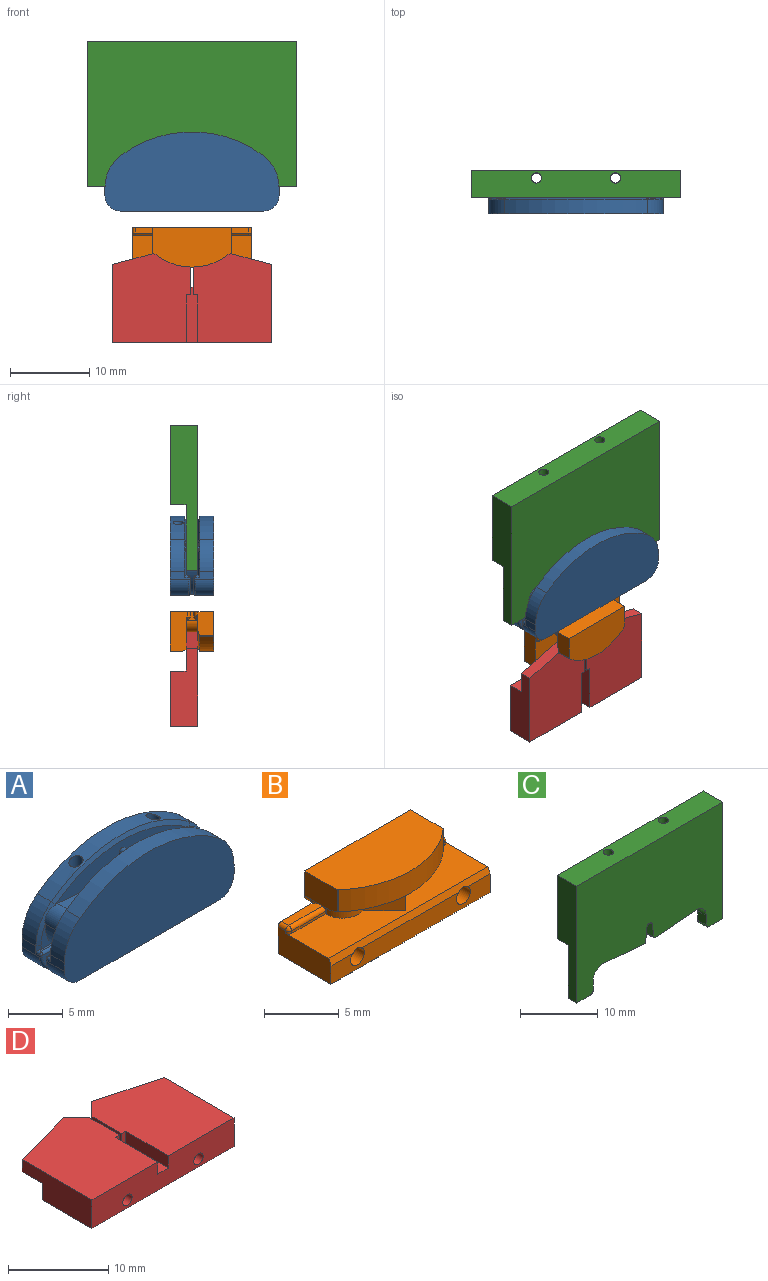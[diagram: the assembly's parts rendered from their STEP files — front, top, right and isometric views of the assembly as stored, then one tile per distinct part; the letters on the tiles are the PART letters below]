
ASSEMBLY  parts=4 mates=3
PART A: 86 faces, bbox 22.4x5.6x10.2 mm
  f0: plane 4.8x2mm, normal (0,1,0), area 5mm2, adj f8,f42,f82,f83,f84
  f1: plane 4.8x2mm, normal (0,-1,0), area 5mm2, adj f8,f46,f71,f72,f73
  f2: plane 2.56x1.23mm, normal (0,-1,0), area 1.6mm2, adj f8,f26,f56,f57
  f3: plane 2.56x1.23mm, normal (0,-1,0), area 1.6mm2, adj f9,f27,f53,f54
  f4: plane 2.56x1.23mm, normal (0,1,0), area 1.6mm2, adj f9,f38,f51,f52
  f5: plane 2.56x1.23mm, normal (0,1,0), area 1.6mm2, adj f8,f37,f48,f49
  f6: plane 17.45x3.56mm, normal (0,1,0), area 38.3mm2, adj f15,f16,f17,f18,f19,f20,f21,f22
  f7: plane 10x0.5mm, normal (0,0,-1), area 5mm2, adj f8,f9,f69,f80
  f8: cylinder r=5mm len=5mm, axis (0,1,0), area 6.7mm2, adj f0,f1,f2,f5,f7,f21,f26,f37
  f9: cylinder r=5mm len=5mm, axis (0,1,0), area 6.7mm2, adj f3,f4,f7,f22,f27,f28,f38,f39
  f10: plane 2.3x1mm, normal (-1,0,0), area 1.9mm2, adj f12,f34,f43,f48,f62,f84
  f11: plane 2.3x1mm, normal (1,0,0), area 1.9mm2, adj f12,f33,f40,f52,f63,f76
  f12: plane 22x10mm, normal (0,-1,0), area 184.3mm2, adj f10,f11,f30,f32,f33,f34,f62,f63
  f13: plane 17.45x3.56mm, normal (0,-1,0), area 38.3mm2, adj f15,f16,f17,f18,f19,f20,f21,f22
  f14: plane 22x10mm, normal (0,1,0), area 184.3mm2, adj f24,f25,f29,f31,f35,f36,f60,f61
  f15: cylinder r=0.5mm len=1.5mm, axis (0,1,0), area 1.2mm2, adj f6,f13,f16,f23
  f16: plane 1.94x1.5mm, normal (1,0,0.04), area 2.9mm2, adj f6,f13,f15,f17
  f17: cylinder r=0.35mm len=1.5mm, axis (0,1,0), area 1.6mm2, adj f6,f13,f16,f18
  f18: plane 1.94x1.5mm, normal (-1,0,0.04), area 2.9mm2, adj f6,f13,f17,f19
  f19: cylinder r=0.5mm len=1.5mm, axis (0,1,0), area 1.2mm2, adj f6,f13,f18,f20
  f20: plane 7.4x1.5mm, normal (0.09,0,1), area 11.1mm2, adj f6,f13,f19,f21
  f21: cylinder r=1.5mm len=1.63mm, axis (0,1,0), area 3.7mm2, adj f6,f8,f13,f20,f49,f56
  f22: cylinder r=1.5mm len=1.63mm, axis (0,1,0), area 3.7mm2, adj f6,f9,f13,f23,f51,f54
  f23: plane 7.4x1.5mm, normal (-0.09,0,1), area 11.1mm2, adj f6,f13,f15,f22
  f24: plane 2.3x1mm, normal (-1,0,0), area 1.9mm2, adj f14,f36,f47,f57,f61,f73
  f25: plane 2.3x1mm, normal (1,0,0), area 1.9mm2, adj f14,f35,f44,f53,f60,f65
  f26: plane 1.43x0.28mm, normal (0,0,1), area 0.3mm2, adj f2,f8,f46,f47,f57
  f27: plane 1.43x0.28mm, normal (0,0,1), area 0.3mm2, adj f3,f9,f44,f45,f53
  f28: plane 4.8x2mm, normal (0,-1,0), area 5mm2, adj f9,f45,f65,f66,f67
  f29: plane 18x2.33mm, normal (0,0,-1), area 39mm2, adj f14,f58,f59,f60,f61,f67,f68,f69
  f30: plane 18x2.33mm, normal (0,0,-1), area 41.7mm2, adj f12,f62,f63,f78,f79,f80,f81,f82
  f31: cylinder r=15mm len=18mm, axis (0,-1,0), area 31.9mm2, adj f14,f35,f36,f55,f58,f59
  f32: cylinder r=15mm len=18mm, axis (0,-1,0), area 34.7mm2, adj f12,f33,f34,f50
  f33: cylinder r=5mm len=4mm, axis (0,-1,0), area 8.3mm2, adj f11,f12,f32,f51
  f34: cylinder r=5mm len=4mm, axis (0,-1,0), area 8.3mm2, adj f10,f12,f32,f49
  f35: cylinder r=5mm len=4mm, axis (0,-1,0), area 8.3mm2, adj f14,f25,f31,f54
  f36: cylinder r=5mm len=4mm, axis (0,-1,0), area 8.3mm2, adj f14,f24,f31,f56
  f37: plane 1.43x0.28mm, normal (0,0,1), area 0.3mm2, adj f5,f8,f42,f43,f48
  f38: plane 1.43x0.28mm, normal (0,0,1), area 0.3mm2, adj f4,f9,f40,f41,f52
  f39: plane 4.8x2mm, normal (0,1,0), area 5mm2, adj f9,f41,f76,f77,f78
  f40: cylinder r=0.3mm len=0.5mm, axis (0,1,0), area 0.2mm2, adj f11,f38,f52,f75
  f41: cylinder r=0.3mm len=1.73mm, axis (1,0,0), area 0.7mm2, adj f9,f38,f39,f75
  f42: cylinder r=0.3mm len=1.73mm, axis (1,0,0), area 0.7mm2, adj f0,f8,f37,f85
  f43: cylinder r=0.3mm len=0.5mm, axis (0,-1,0), area 0.2mm2, adj f10,f37,f48,f85
  f44: cylinder r=0.3mm len=0.5mm, axis (0,-1,0), area 0.2mm2, adj f25,f27,f53,f64
  f45: cylinder r=0.3mm len=1.73mm, axis (-1,0,0), area 0.7mm2, adj f9,f27,f28,f64
  f46: cylinder r=0.3mm len=1.73mm, axis (-1,0,0), area 0.7mm2, adj f1,f8,f26,f74
  f47: cylinder r=0.3mm len=0.5mm, axis (0,1,0), area 0.2mm2, adj f24,f26,f57,f74
  f48: plane 0.85x0.55mm, normal (-0.37,0.93,0), area 0.3mm2, adj f5,f10,f37,f43,f49
  f49: cone r=4.5mm half-angle=68.2deg, axis (0,-1,0), area 2mm2, adj f5,f6,f8,f21,f34,f48,f50
  f50: cone r=15mm half-angle=68.2deg, axis (0,-1,0), area 10.2mm2, adj f6,f32,f49,f51
  f51: cone r=4.5mm half-angle=68.2deg, axis (0,-1,0), area 2mm2, adj f4,f6,f9,f22,f33,f50,f52
  f52: plane 0.85x0.55mm, normal (0.37,0.93,0), area 0.3mm2, adj f4,f11,f38,f40,f51
  f53: plane 0.85x0.55mm, normal (0.37,-0.93,0), area 0.3mm2, adj f3,f25,f27,f44,f54
  f54: cone r=4.5mm half-angle=68.2deg, axis (0,1,0), area 2mm2, adj f3,f9,f13,f22,f35,f53,f55
  f55: cone r=15mm half-angle=68.2deg, axis (0,1,0), area 10.2mm2, adj f13,f31,f54,f56
  f56: cone r=4.5mm half-angle=68.2deg, axis (0,1,0), area 2mm2, adj f2,f8,f13,f21,f36,f55,f57
  f57: plane 0.85x0.55mm, normal (-0.37,-0.93,0), area 0.3mm2, adj f2,f24,f26,f47,f56
  f58: cylinder r=0.65mm len=9.36mm, axis (0,0,-1), area 37.3mm2, adj f29,f31
  f59: cylinder r=0.65mm len=9.36mm, axis (0,0,-1), area 37.3mm2, adj f29,f31
  f60: cylinder r=2mm len=2.3mm, axis (0,1,0), area 7.2mm2, adj f14,f25,f29,f66
  f61: cylinder r=2mm len=2.3mm, axis (0,-1,0), area 7.2mm2, adj f14,f24,f29,f72
  f62: cylinder r=2mm len=2.3mm, axis (0,1,0), area 7.2mm2, adj f10,f12,f30,f83
  f63: cylinder r=2mm len=2.3mm, axis (0,-1,0), area 7.2mm2, adj f11,f12,f30,f77
  f64: bspline ~0.36x0.3mm, area 0.1mm2, adj f44,f45,f65
  f65: cylinder r=0.2mm len=0.2mm, axis (0,0,-1), area 0.1mm2, adj f25,f28,f64,f66
  f66: torus R=1.8mm, axis (0,1,0), area 1mm2, adj f28,f60,f65,f67
  f67: cylinder r=0.2mm len=3mm, axis (1,0,0), area 0.9mm2, adj f28,f29,f66,f68
  f68: bspline ~1.36x0.22mm, area 0.2mm2, adj f9,f29,f67,f69
  f69: cylinder r=0.2mm len=10mm, axis (1,0,0), area 2.1mm2, adj f7,f29,f68,f70
  f70: bspline ~1.42x0.23mm, area 0.2mm2, adj f8,f29,f69,f71
  f71: cylinder r=0.2mm len=3mm, axis (1,0,0), area 0.9mm2, adj f1,f29,f70,f72
  f72: torus R=1.8mm, axis (0,1,0), area 1mm2, adj f1,f61,f71,f73
  f73: cylinder r=0.2mm len=0.2mm, axis (0,0,1), area 0.1mm2, adj f1,f24,f72,f74
  f74: bspline ~0.36x0.3mm, area 0.1mm2, adj f46,f47,f73
  f75: bspline ~0.36x0.3mm, area 0.1mm2, adj f40,f41,f76
  f76: cylinder r=0.2mm len=0.2mm, axis (0,0,1), area 0.1mm2, adj f11,f39,f75,f77
  f77: torus R=1.8mm, axis (0,-1,0), area 1mm2, adj f39,f63,f76,f78
  f78: cylinder r=0.2mm len=3mm, axis (-1,0,0), area 0.9mm2, adj f30,f39,f77,f79
  f79: bspline ~1.42x0.23mm, area 0.2mm2, adj f9,f30,f78,f80
  f80: cylinder r=0.2mm len=10mm, axis (-1,0,0), area 2.1mm2, adj f7,f30,f79,f81
  f81: bspline ~1.36x0.22mm, area 0.2mm2, adj f8,f30,f80,f82
  f82: cylinder r=0.2mm len=3mm, axis (-1,0,0), area 0.9mm2, adj f0,f30,f81,f83
  f83: torus R=1.8mm, axis (0,-1,0), area 1mm2, adj f0,f62,f82,f84
  f84: cylinder r=0.2mm len=0.2mm, axis (0,0,-1), area 0.1mm2, adj f0,f10,f83,f85
  f85: bspline ~0.32x0.3mm, area 0.1mm2, adj f42,f43,f84
PART B: 50 faces, bbox 15x5x5.5 mm
  f0: plane 5x4mm, normal (0,0,-1), area 6.6mm2, adj f7,f8,f9,f10,f23,f27,f29,f47
  f1: plane 5x4mm, normal (0,0,-1), area 6.6mm2, adj f4,f11,f12,f13,f14,f26,f29,f44
  f2: plane 15x5.5mm, normal (0,1,0), area 63.7mm2, adj f3,f5,f10,f11,f15,f17,f18,f20
  f3: plane 10x5mm, normal (0,0,1), area 44mm2, adj f2,f25,f26,f27,f48,f49
  f4: plane 0.5x0.2mm, normal (0,-1,0), area 0.1mm2, adj f1,f11,f38,f44
  f5: plane 0.7x0.5mm, normal (0,0,-1), area 0.3mm2, adj f2,f11,f38,f42
  f6: plane 15x4.1mm, normal (0,0,1), area 41.7mm2, adj f7,f8,f9,f10,f11,f12,f13,f14
  f7: plane 2x2mm, normal (0.71,-0.71,0), area 4.2mm2, adj f0,f6,f8,f14
  f8: plane 1.5x0.11mm, normal (-0.26,-0.97,0), area 0.2mm2, adj f0,f6,f7,f9
  f9: cylinder r=1.5mm len=1.89mm, axis (0,0,-1), area 4.1mm2, adj f0,f6,f8,f10
  f10: plane 1.5x1.08mm, normal (1,0,0), area 0.7mm2, adj f0,f2,f6,f9,f21,f22,f23,f24
  f11: plane 1.5x1.08mm, normal (-1,0,0), area 0.7mm2, adj f1,f2,f4,f5,f6,f12,f19,f20
  f12: cylinder r=1.5mm len=1.89mm, axis (0,0,-1), area 4.1mm2, adj f1,f6,f11,f13
  f13: plane 1.5x0.11mm, normal (0.26,-0.97,0), area 0.2mm2, adj f1,f6,f12,f14
  f14: plane 2x2mm, normal (-0.71,-0.71,0), area 4.2mm2, adj f1,f6,f7,f13
  f15: plane 5x2.2mm, normal (1,0,0), area 10.1mm2, adj f2,f6,f16,f18,f28,f30,f33
  f16: plane 15x1.5mm, normal (0,-1,0), area 20mm2, adj f15,f17,f18,f28,f40,f41
  f17: plane 5x2.2mm, normal (-1,0,0), area 10.1mm2, adj f2,f6,f16,f18,f28,f35,f37
  f18: plane 15x5mm, normal (0,0,-1), area 75mm2, adj f2,f15,f16,f17
  f19: plane 3.2x0.2mm, normal (0,-1,0), area 0.6mm2, adj f6,f11,f34,f35
  f20: plane 3.2x0.7mm, normal (0,0,1), area 2.2mm2, adj f2,f11,f34,f37
  f21: plane 3.2x0.2mm, normal (0,-1,0), area 0.6mm2, adj f6,f10,f30,f31
  f22: plane 3.2x0.7mm, normal (0,0,1), area 2.2mm2, adj f2,f10,f31,f33
  f23: plane 0.5x0.2mm, normal (0,-1,0), area 0.1mm2, adj f0,f10,f39,f47
  f24: plane 0.7x0.5mm, normal (0,0,-1), area 0.3mm2, adj f2,f10,f39,f45
  f25: cylinder r=7.5mm len=9.92mm, axis (0,0,1), area 19.5mm2, adj f3,f29,f48,f49
  f26: plane 3.11x2.02mm, normal (-1,0,0), area 6.1mm2, adj f1,f2,f3,f29,f42,f48
  f27: plane 3.11x2.02mm, normal (1,0,0), area 6.1mm2, adj f0,f2,f3,f29,f45,f49
  f28: plane 15x0.5mm, normal (0,-0.93,0.37), area 7.9mm2, adj f6,f15,f16,f17,f40,f41
  f29: cone r=7.5mm half-angle=68.2deg, axis (0,0,1), area 6mm2, adj f0,f1,f25,f26,f27,f48,f49
  f30: cylinder r=0.3mm len=0.3mm, axis (0,0,1), area 0.1mm2, adj f6,f15,f21,f32
  f31: cylinder r=0.3mm len=3.2mm, axis (-1,0,0), area 1.5mm2, adj f10,f21,f22,f32
  f32: sphere r=0.3mm, area 0.1mm2, adj f30,f31,f33
  f33: cylinder r=0.3mm len=0.7mm, axis (0,1,0), area 0.3mm2, adj f2,f15,f22,f32
  f34: cylinder r=0.3mm len=3.2mm, axis (-1,0,0), area 1.5mm2, adj f11,f19,f20,f36
  f35: cylinder r=0.3mm len=0.3mm, axis (0,0,-1), area 0.1mm2, adj f6,f17,f19,f36
  f36: sphere r=0.3mm, area 0.1mm2, adj f34,f35,f37
  f37: cylinder r=0.3mm len=0.7mm, axis (0,1,0), area 0.3mm2, adj f2,f17,f20,f36
  f38: cylinder r=0.3mm len=0.5mm, axis (1,0,0), area 0.2mm2, adj f4,f5,f11,f43
  f39: cylinder r=0.3mm len=0.5mm, axis (1,0,0), area 0.2mm2, adj f10,f23,f24,f46
  f40: cylinder r=0.65mm len=5mm, axis (0,1,0), area 20.4mm2, adj f2,f16,f28
  f41: cylinder r=0.65mm len=5mm, axis (0,1,0), area 20.4mm2, adj f2,f16,f28
  f42: cylinder r=0.5mm len=0.7mm, axis (0,1,0), area 0.5mm2, adj f2,f5,f26,f43
  f43: bspline ~0.6x0.5mm, area 0.2mm2, adj f38,f42,f44
  f44: cylinder r=0.5mm len=0.5mm, axis (0,0,-1), area 0.1mm2, adj f1,f4,f43
  f45: cylinder r=0.5mm len=0.7mm, axis (0,-1,0), area 0.5mm2, adj f2,f24,f27,f46
  f46: bspline ~0.6x0.5mm, area 0.2mm2, adj f39,f45,f47
  f47: cylinder r=0.5mm len=0.5mm, axis (0,0,1), area 0.1mm2, adj f0,f23,f46
  f48: cylinder r=0.5mm len=1.8mm, axis (0,0,-1), area 0.1mm2, adj f3,f25,f26,f29
  f49: cylinder r=0.5mm len=1.8mm, axis (0,0,-1), area 0.1mm2, adj f3,f25,f27,f29
PART C: 24 faces, bbox 26.5x3.5x18.3 mm
  f0: plane 26.5x3.5mm, normal (0,0,1), area 90.1mm2, adj f1,f17,f18,f21,f22,f23
  f1: plane 18.33x3.5mm, normal (-1,0,0), area 47.5mm2, adj f0,f2,f18,f19,f20,f21
  f2: plane 2.5x1.5mm, normal (0,0,-1), area 3.8mm2, adj f1,f3,f18,f19
  f3: cylinder r=0.5mm len=1.5mm, axis (0,1,0), area 1.2mm2, adj f2,f4,f18,f19
  f4: plane 1.5x1.5mm, normal (1,0,0), area 2.2mm2, adj f3,f5,f18,f19
  f5: cylinder r=1.8mm len=1.96mm, axis (0,1,0), area 4.5mm2, adj f4,f6,f18,f19
  f6: plane 7.3x1.5mm, normal (-0.09,0,-1), area 11mm2, adj f5,f7,f18,f19
  f7: cylinder r=0.25mm len=1.5mm, axis (0,1,0), area 0.6mm2, adj f6,f8,f18,f19
  f8: plane 2.11x1.5mm, normal (0.99,0,-0.11), area 3.2mm2, adj f7,f9,f18,f19
  f9: cylinder r=0.5mm len=1.5mm, axis (0,1,0), area 2.2mm2, adj f8,f10,f18,f19
  f10: plane 2.11x1.5mm, normal (-0.99,0,-0.11), area 3.2mm2, adj f9,f11,f18,f19
  f11: cylinder r=0.25mm len=1.5mm, axis (0,1,0), area 0.6mm2, adj f10,f12,f18,f19
  f12: plane 7.3x1.5mm, normal (0.09,0,-1), area 11mm2, adj f11,f13,f18,f19
  f13: cylinder r=1.8mm len=1.96mm, axis (0,1,0), area 4.5mm2, adj f12,f14,f18,f19
  f14: plane 1.5x1.5mm, normal (-1,0,0), area 2.2mm2, adj f13,f15,f18,f19
  f15: cylinder r=0.5mm len=1.5mm, axis (0,1,0), area 1.2mm2, adj f14,f16,f18,f19
  f16: plane 2.5x1.5mm, normal (0,0,-1), area 3.8mm2, adj f15,f17,f18,f19
  f17: plane 18.33x3.5mm, normal (1,0,0), area 47.5mm2, adj f0,f16,f18,f19,f20,f21
  f18: plane 26.5x18.33mm, normal (0,-1,0), area 411.8mm2, adj f0,f1,f2,f3,f4,f5,f6,f7
  f19: plane 26.5x8.33mm, normal (0,1,0), area 146.8mm2, adj f1,f2,f3,f4,f5,f6,f7,f8
  f20: plane 26.5x2mm, normal (0,0,-1), area 50.3mm2, adj f1,f17,f19,f21,f22,f23
  f21: plane 26.5x10mm, normal (0,1,0), area 265mm2, adj f0,f1,f17,f20
  f22: cylinder r=0.65mm len=10mm, axis (0,0,1), area 40.8mm2, adj f0,f20
  f23: cylinder r=0.65mm len=10mm, axis (0,0,1), area 40.8mm2, adj f0,f20
PART D: 22 faces, bbox 20x12x3.5 mm
  f0: plane 20x7mm, normal (0,0,-1), area 140mm2, adj f3,f4,f6,f19
  f1: plane 7x1.5mm, normal (0,0,1), area 9.3mm2, adj f5,f6,f8,f9,f10,f11,f12,f19
  f2: plane 12x9.85mm, normal (0,0,1), area 104.3mm2, adj f4,f5,f6,f10,f11,f13,f14
  f3: plane 9.86x3.5mm, normal (1,0,0), area 28.8mm2, adj f0,f6,f7,f16,f17,f19
  f4: plane 9.86x3.5mm, normal (-1,0,0), area 28.8mm2, adj f0,f2,f6,f14,f18,f19
  f5: plane 4.15x1.5mm, normal (1,0,0), area 6.2mm2, adj f1,f2,f10,f13,f18
  f6: plane 20x3.5mm, normal (0,-1,0), area 65.1mm2, adj f0,f1,f2,f3,f4,f7,f11,f12
  f7: plane 12x9.85mm, normal (0,0,1), area 104.3mm2, adj f3,f6,f8,f9,f12,f15,f16
  f8: plane 4.15x1.5mm, normal (-1,0,0), area 6.2mm2, adj f1,f7,f9,f15,f17
  f9: plane 1.5x0.6mm, normal (0,-1,0), area 0.9mm2, adj f1,f7,f8,f12
  f10: plane 1.5x0.6mm, normal (0,-1,0), area 0.9mm2, adj f1,f2,f5,f11
  f11: plane 6x1.5mm, normal (1,0,0), area 9mm2, adj f1,f2,f6,f10
  f12: plane 6x1.5mm, normal (-1,0,0), area 9mm2, adj f1,f6,f7,f9
  f13: plane 1.85x1.85mm, normal (0.71,0.71,0), area 3.9mm2, adj f2,f5,f14,f18
  f14: plane 8x2.14mm, normal (-0.26,0.97,0), area 12.4mm2, adj f2,f4,f13,f18
  f15: plane 1.85x1.85mm, normal (-0.71,0.71,0), area 3.9mm2, adj f7,f8,f16,f17
  f16: plane 8x2.14mm, normal (0.26,0.97,0), area 12.4mm2, adj f3,f7,f15,f17
  f17: plane 9.85x5mm, normal (0,0,-1), area 39mm2, adj f3,f8,f15,f16,f19
  f18: plane 9.85x5mm, normal (0,0,-1), area 39mm2, adj f4,f5,f13,f14,f19
  f19: plane 20x2mm, normal (0,1,0), area 37.3mm2, adj f0,f1,f3,f4,f17,f18,f20,f21
  f20: cylinder r=0.65mm len=7mm, axis (0,-1,0), area 28.6mm2, adj f6,f19
  f21: cylinder r=0.65mm len=7mm, axis (0,-1,0), area 28.6mm2, adj f6,f19
PLACE A t=(8.9,33.02,53.34)mm
PLACE B rot(axis=(1,0,0),90deg) t=(8.9,33.02,43.75)mm
PLACE C t=(8.9,33.02,45.75)mm
PLACE D rot(axis=(1,0,0),90deg) t=(8.9,35.02,39.74)mm
MATE slider A.f58 <-> B.f41  axis (0,0,-1) through (3.9,34.02,50.34)mm
MATE slider B.f41 <-> D.f21  axis (0,0,1) through (3.9,34.02,43.25)mm
MATE slider C.f23 <-> A.f58  axis (0,0,-1) through (3.9,34.02,61.75)mm
